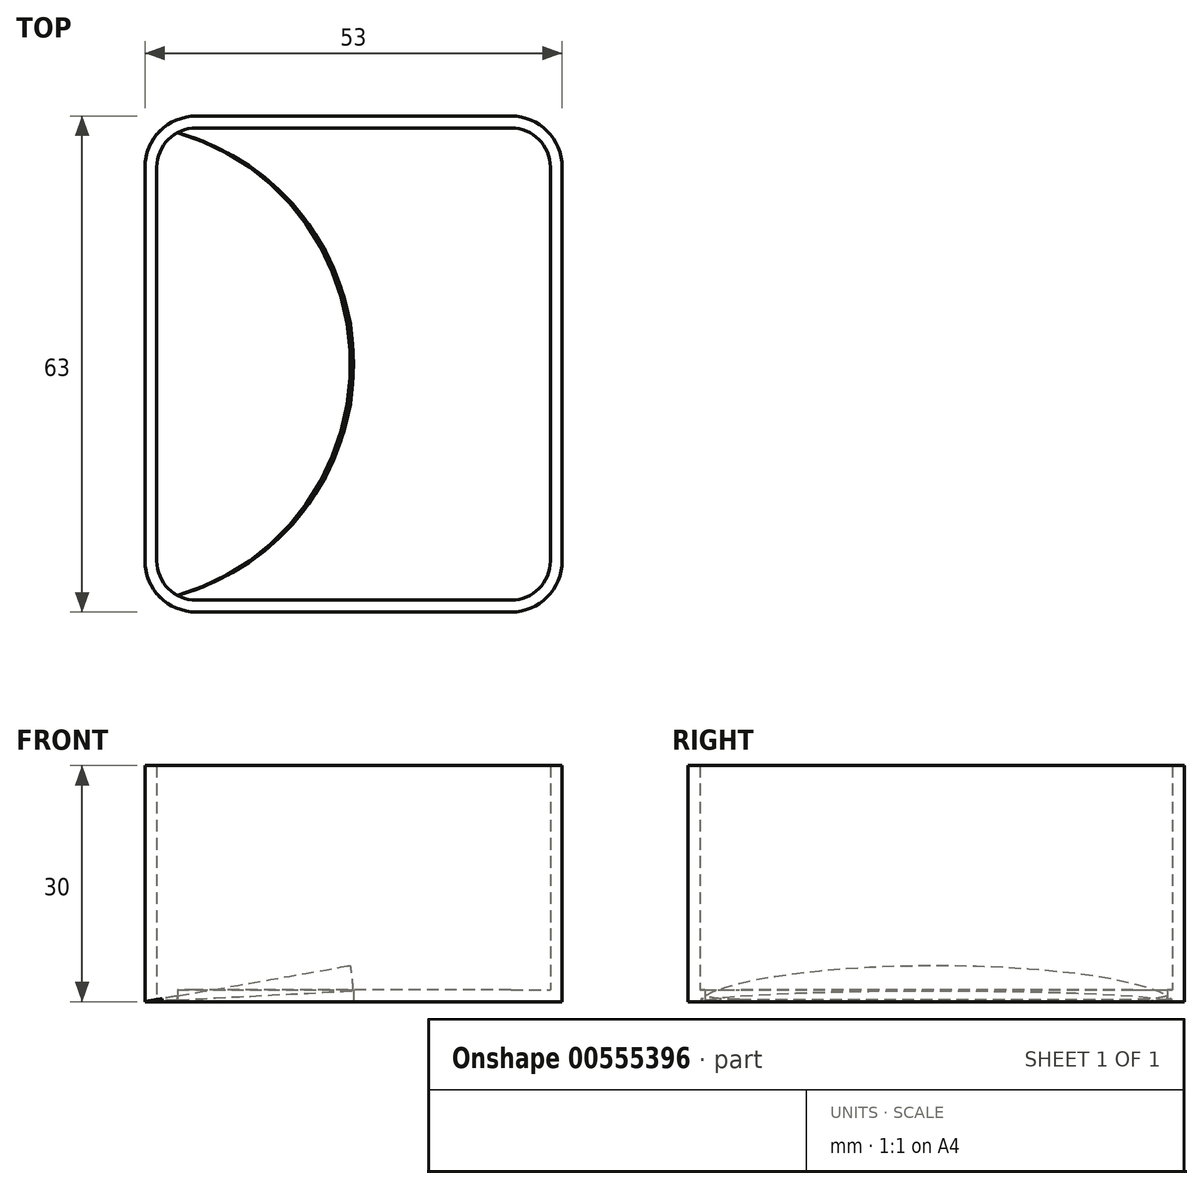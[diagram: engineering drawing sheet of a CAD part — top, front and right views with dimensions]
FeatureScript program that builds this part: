
annotation { "Feature Type Name" : "Feature", "Feature Type Description" : "" }
export const myFeature = defineFeature(function(context is Context, id is Id, definition is map)
    precondition{}
    {
        {
            var Q0;
            Q0=qCreatedBy(makeId("Top.planeOp"),FACE);
            var sketch = newSketch(context, id + "F0", { "sketchPlane" : qUnion([Q0])});
            skLineSegment(sketch, "E0.bottom", {"start": v(20, 30) * mm, "end": v(-20, 30) * mm});
            skLineSegment(sketch, "E0.top", {"start": v(20, -30) * mm, "end": v(-20, -30) * mm});
            skLineSegment(sketch, "E0.left", {"start": v(25, 25) * mm, "end": v(25, -25) * mm});
            skLineSegment(sketch, "E0.right", {"start": v(-25, 25) * mm, "end": v(-25, -25) * mm});
            skPoint(sketch, "E0.middle", {"position": v(0, 0) * mm});
            skPoint(sketch, "E1.visualSharp", {"position": v(-25, 30) * mm});
            skArc(sketch, "E1.filletArc", {"start": v(-20, 30) * mm, "mid": v(-23.54, 28.54) * mm, "end": v(-25, 25) * mm});
            skPoint(sketch, "E2.visualSharp", {"position": v(25, 30) * mm});
            skArc(sketch, "E2.filletArc", {"start": v(25, 25) * mm, "mid": v(23.54, 28.54) * mm, "end": v(20, 30) * mm});
            skPoint(sketch, "E3.visualSharp", {"position": v(-25, -30) * mm});
            skArc(sketch, "E3.filletArc", {"start": v(-25, -25) * mm, "mid": v(-23.54, -28.54) * mm, "end": v(-20, -30) * mm});
            skPoint(sketch, "E4.visualSharp", {"position": v(25, -30) * mm});
            skArc(sketch, "E4.filletArc", {"start": v(20, -30) * mm, "mid": v(23.54, -28.54) * mm, "end": v(25, -25) * mm});
            skLineSegment(sketch, "E5.0", {"start": v(-26.5, 25) * mm, "end": v(-26.5, -25) * mm});
            skArc(sketch, "E6.0", {"start": v(-20, 31.5) * mm, "mid": v(-24.6, 29.6) * mm, "end": v(-26.5, 25) * mm});
            skLineSegment(sketch, "E6.1", {"start": v(20, 31.5) * mm, "end": v(-20, 31.5) * mm});
            skArc(sketch, "E6.2", {"start": v(26.5, 25) * mm, "mid": v(24.6, 29.6) * mm, "end": v(20, 31.5) * mm});
            skArc(sketch, "E6.3", {"start": v(-26.5, -25) * mm, "mid": v(-24.6, -29.6) * mm, "end": v(-20, -31.5) * mm});
            skLineSegment(sketch, "E6.4", {"start": v(20, -31.5) * mm, "end": v(-20, -31.5) * mm});
            skArc(sketch, "E6.5", {"start": v(20, -31.5) * mm, "mid": v(24.6, -29.6) * mm, "end": v(26.5, -25) * mm});
            skLineSegment(sketch, "E6.6", {"start": v(26.5, 25) * mm, "end": v(26.5, -25) * mm});
            skArc(sketch, "E7", {"start": v(-25, -30) * mm, "mid": v(0, 0) * mm, "end": v(-25, 30) * mm});
            skSolve(sketch);
        }
        {
            var Q0;
            Q0=makeQuery(id+"F0.imprint","IMPRINT",FACE,{"disambiguationData":[TD([[makeQuery(id+"F0.imprint","IMPRINT",EDGE,{"derivedFrom":sQuery(id+"F0.wireOp",EDGE,"E0.bottom")}),1.0]])]});
            extrude(context, id + "F1", {"entities" : qUnion([Q0]), "depth" : 1.5 * mm, "offsetDistance" : 25 * mm});
        }
        {
            var Q0;
            {var subQ7=sQuery(id+"F0.wireOp",EDGE,"E0.bottom");Q0=makeQuery(id+"F0.imprint","IMPRINT",FACE,{"disambiguationData":[TD([[makeQuery(id+"F0.imprint","IMPRINT",EDGE,{"derivedFrom":subQ7}),-1.0]])]});}
            extrude(context, id + "F2", {"entities" : qUnion([Q0]), "operationType" : NewBodyOperationType.ADD, "depth" : 30 * mm, "offsetDistance" : 25 * mm});
        }
        {
            var Q0;
            {var subQ0=sQuery(id+"F0.wireOp",EDGE,"E0.right");Q0=makeQuery(id+"F0.imprint","IMPRINT",FACE,{"disambiguationData":[TD([[makeQuery(id+"F0.imprint","IMPRINT",EDGE,{"derivedFrom":subQ0}),1.0]])]});}
            var Q1;
            {var subQ1=sQuery(id+"F0.wireOp",EDGE,"E0.right");Q1=makeQuery(id+"F0.imprint","IMPRINT",FACE,{"disambiguationData":[TD([[makeQuery(id+"F0.imprint","IMPRINT",EDGE,{"derivedFrom":subQ1}),-1.0]])]});}
            var Q2;
            Q2=sQuery(id+"F0.wireOp",EDGE,"E5.0");
            revolve(context, id + "F3", {"entities" : qUnion([Q0, Q1]), "axis" : qUnion([Q2]), "revolveType" : RevolveType.ONE_DIRECTION, "angle" : 7 * degree});
        }
        {
            var Q0;
            Q0=makeQuery(id+"F3.opRevolve","CAP_EDGE",EDGE,{"disambiguationData":[OSD([sQuery(id+"F0.wireOp",EDGE,"E5.0")])],"isStart":true});
            cPoint(context, id + "F4", {"entities" : qUnion([Q0]), "parameter" : 0.5});
        }
        {
            var Q0;
            Q0=makeQuery(id+"F3.opRevolve","SWEPT_BODY",BODY,{"disambiguationData":[OSD([sQuery(id+"F0.wireOp",EDGE,"E5.0"),sQuery(id+"F0.wireOp",EDGE,"E6.0"),sQuery(id+"F0.wireOp",EDGE,"E6.3"),sQuery(id+"F0.wireOp",EDGE,"E7")])]});
            var Q1;
            Q1 = qCreatedBy(id + "F4" ,VERTEX);
            var Q2;
            Q2=makeQuery(id+"F3.opRevolve","CAP_EDGE",EDGE,{"disambiguationData":[OSD([sQuery(id+"F0.wireOp",EDGE,"E5.0")])],"isStart":true});
            transform(context, id + "F5", {"entities" : qUnion([Q0]), "transformType" : TransformType.ROTATION, "transformAxis" : qUnion([Q2]), "angle" : 3 * degree, "makeCopy" : false});
        }
        {
            var Q0;
            Q0 = qSketchRegion(id + "F0", true);
            extrude(context, id + "F6", {"entities" : qUnion([Q0]), "operationType" : NewBodyOperationType.ADD, "depth" : 30 * mm, "offsetDistance" : 25 * mm});
        }
    });
